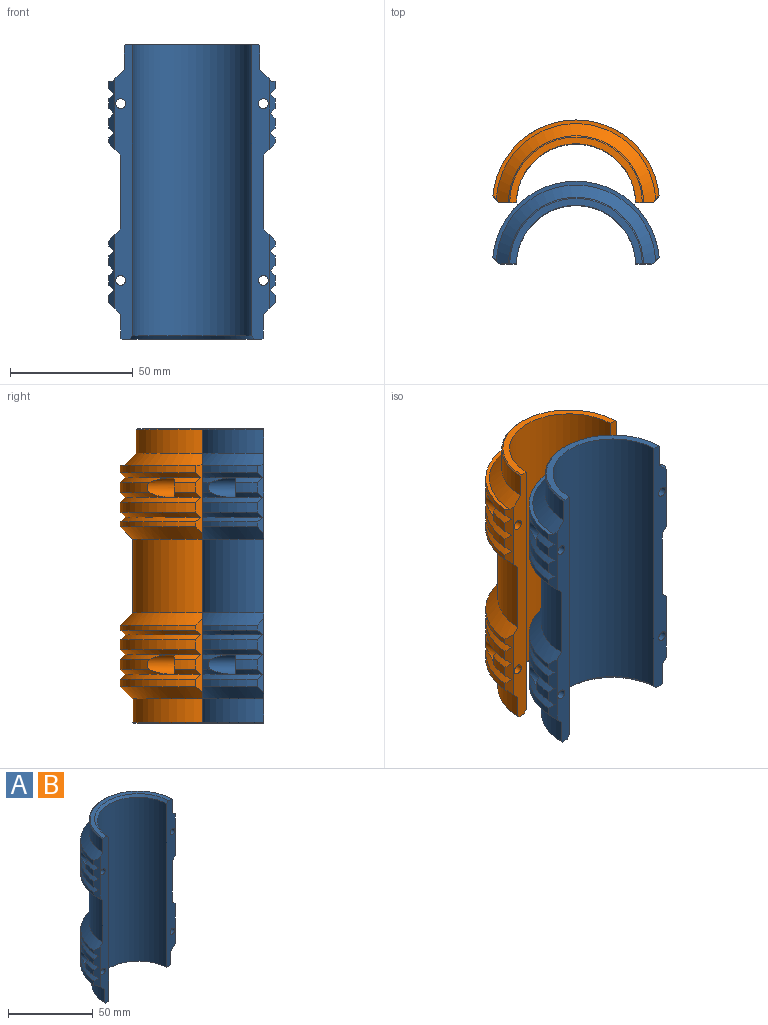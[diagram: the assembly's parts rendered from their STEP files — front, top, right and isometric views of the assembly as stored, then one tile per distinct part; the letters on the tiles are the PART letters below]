
ASSEMBLY  parts=2 mates=1
PART A: 64 faces, bbox 68.1x33.7x120.1 mm
  f0: cone r=32mm half-angle=45deg, axis (0,0,1), area 175.5mm2, adj f4,f42,f54,f60
  f1: cone r=35mm half-angle=45deg, axis (0,0,-1), area 175.5mm2, adj f4,f43,f54,f60
  f2: cone r=32mm half-angle=45deg, axis (0,0,1), area 175.5mm2, adj f7,f48,f52,f58
  f3: cone r=35mm half-angle=45deg, axis (0,0,-1), area 175.5mm2, adj f7,f49,f52,f58
  f4: cylinder r=34mm len=51.17mm, axis (0,0,-1), area 227.3mm2, adj f0,f1,f54,f60
  f5: cylinder r=34mm len=8.81mm, axis (0,0,-1), area 36.3mm2, adj f8,f10,f40,f61
  f6: cylinder r=34mm len=8.81mm, axis (0,0,-1), area 36.3mm2, adj f12,f14,f41,f59
  f7: cylinder r=34mm len=51.17mm, axis (0,0,-1), area 227.3mm2, adj f2,f3,f52,f58
  f8: cone r=32mm half-angle=45deg, axis (0,0,1), area 28.7mm2, adj f5,f40,f42,f60,f61
  f9: cone r=32mm half-angle=45deg, axis (0,0,1), area 28.7mm2, adj f20,f39,f42,f54,f55
  f10: cone r=35mm half-angle=45deg, axis (0,0,-1), area 28.7mm2, adj f5,f40,f43,f60,f61
  f11: cone r=35mm half-angle=45deg, axis (0,0,-1), area 28.7mm2, adj f20,f39,f43,f54,f55
  f12: cone r=32mm half-angle=45deg, axis (0,0,1), area 28.7mm2, adj f6,f41,f48,f58,f59
  f13: cone r=32mm half-angle=45deg, axis (0,0,1), area 28.7mm2, adj f16,f38,f48,f52,f53
  f14: cone r=35mm half-angle=45deg, axis (0,0,-1), area 28.7mm2, adj f6,f41,f49,f58,f59
  f15: cone r=35mm half-angle=45deg, axis (0,0,-1), area 28.7mm2, adj f16,f38,f49,f52,f53
  f16: cylinder r=34mm len=8.81mm, axis (0,0,-1), area 36.3mm2, adj f13,f15,f38,f53
  f17: cylinder r=34mm len=67.7mm, axis (0,0,-1), area 401.7mm2, adj f38,f41,f47,f48
  f18: cylinder r=34mm len=67.7mm, axis (0,0,-1), area 200.8mm2, adj f37,f38,f41,f46
  f19: cylinder r=34mm len=67.7mm, axis (0,0,-1), area 401.7mm2, adj f39,f40,f43,f44
  f20: cylinder r=34mm len=8.81mm, axis (0,0,-1), area 36.3mm2, adj f9,f11,f39,f55
  f21: cylinder r=34mm len=67.7mm, axis (0,0,-1), area 301.2mm2, adj f29,f39,f40,f42
  f22: plane 120x7.16mm, normal (0,-1,0), area 680.4mm2, adj f24,f25,f26,f27,f30,f31,f32,f34
  f23: cylinder r=34mm len=67.7mm, axis (0,0,-1), area 301.2mm2, adj f36,f38,f41,f49
  f24: cone r=24.25mm half-angle=45deg, axis (0,0,1), area 164.5mm2, adj f22,f25,f30,f33
  f25: cylinder r=24.25mm len=118.5mm, axis (0,0,1), area 8909.3mm2, adj f22,f24,f26,f33
  f26: plane 53.99x26.5mm, normal (0,0,-1), area 218.6mm2, adj f22,f25,f33,f62
  f27: cylinder r=27.5mm len=54.99mm, axis (0,0,-1), area 811.2mm2, adj f22,f33,f34,f62
  f28: cylinder r=34mm len=67.7mm, axis (0,0,-1), area 200.8mm2, adj f35,f39,f40,f45
  f29: plane 67.7x32.34mm, normal (0,0,-1), area 149.4mm2, adj f21,f34,f39,f40
  f30: plane 56.99x28mm, normal (0,0,1), area 231.6mm2, adj f22,f24,f33,f63
  f31: cylinder r=29mm len=57.99mm, axis (0,0,-1), area 856mm2, adj f22,f33,f36,f63
  f32: cylinder r=29mm len=57.99mm, axis (0,0,-1), area 2703.2mm2, adj f22,f33,f35,f37
  f33: plane 120x7.16mm, normal (0,-1,0), area 680.4mm2, adj f24,f25,f26,f27,f30,f31,f32,f34
  f34: cone r=27.5mm half-angle=45deg, axis (0,0,1), area 657.6mm2, adj f22,f27,f29,f33,f39,f40
  f35: cone r=34mm half-angle=45deg, axis (0,0,-1), area 683mm2, adj f22,f28,f32,f33,f39,f40
  f36: cone r=34mm half-angle=45deg, axis (0,0,-1), area 683mm2, adj f22,f23,f31,f33,f38,f41
  f37: cone r=29mm half-angle=45deg, axis (0,0,1), area 683mm2, adj f18,f22,f32,f33,f38,f41
  f38: plane 30.33x2.82mm, normal (-0.74,-0.67,0), area 84.2mm2, adj f13,f15,f16,f17,f18,f23,f33,f36
  f39: plane 28.83x2.82mm, normal (-0.74,-0.67,0), area 80.3mm2, adj f9,f11,f19,f20,f21,f28,f29,f33
  f40: plane 28.83x2.82mm, normal (0.74,-0.67,0), area 80.3mm2, adj f5,f8,f10,f19,f21,f22,f28,f29
  f41: plane 30.33x2.82mm, normal (0.74,-0.67,0), area 84.2mm2, adj f6,f12,f14,f17,f18,f22,f23,f36
  f42: cone r=35mm half-angle=45deg, axis (0,0,-1), area 281.1mm2, adj f0,f8,f9,f21,f39,f40
  f43: cone r=32mm half-angle=45deg, axis (0,0,1), area 281.1mm2, adj f1,f10,f11,f19,f39,f40
  f44: cone r=35mm half-angle=45deg, axis (0,0,-1), area 281.1mm2, adj f19,f39,f40,f45
  f45: cone r=32mm half-angle=45deg, axis (0,0,1), area 281.1mm2, adj f28,f39,f40,f44
  f46: cone r=35mm half-angle=45deg, axis (0,0,-1), area 281.1mm2, adj f18,f38,f41,f47
  f47: cone r=32mm half-angle=45deg, axis (0,0,1), area 281.1mm2, adj f17,f38,f41,f46
  f48: cone r=35mm half-angle=45deg, axis (0,0,-1), area 281.1mm2, adj f2,f12,f13,f17,f38,f41
  f49: cone r=32mm half-angle=45deg, axis (0,0,1), area 281.1mm2, adj f3,f14,f15,f23,f38,f41
  f50: cylinder r=2mm len=11.5mm, axis (0,-1,0), area 144.5mm2, adj f33,f55
  f51: cylinder r=2mm len=11.5mm, axis (0,-1,0), area 144.5mm2, adj f33,f53
  f52: cylinder r=4mm len=10.99mm, axis (0,1,0), area 95.7mm2, adj f2,f3,f7,f13,f15,f53
  f53: plane 8.02x6.79mm, normal (0,1,0), area 30.4mm2, adj f13,f15,f16,f51,f52
  f54: cylinder r=4mm len=10.99mm, axis (0,1,0), area 95.7mm2, adj f0,f1,f4,f9,f11,f55
  f55: plane 8.02x6.79mm, normal (0,1,0), area 30.4mm2, adj f9,f11,f20,f50,f54
  f56: cylinder r=2mm len=11.5mm, axis (0,-1,0), area 144.5mm2, adj f22,f61
  f57: cylinder r=2mm len=11.5mm, axis (0,-1,0), area 144.5mm2, adj f22,f59
  f58: cylinder r=4mm len=10.99mm, axis (0,1,0), area 95.7mm2, adj f2,f3,f7,f12,f14,f59
  f59: plane 8.02x6.79mm, normal (0,1,0), area 30.4mm2, adj f6,f12,f14,f57,f58
  f60: cylinder r=4mm len=10.99mm, axis (0,1,0), area 95.7mm2, adj f0,f1,f4,f8,f10,f61
  f61: plane 8.02x6.79mm, normal (0,1,0), area 30.4mm2, adj f5,f8,f10,f56,f60
  f62: cone r=27mm half-angle=45deg, axis (0,0,1), area 59.8mm2, adj f22,f26,f27,f33
  f63: cone r=29mm half-angle=45deg, axis (0,0,-1), area 63.2mm2, adj f22,f30,f31,f33
PART B: same geometry as A
PLACE A rot(axis=(0,1,0),180deg) t=(-81.18,-34.98,91.7)mm fixed
PLACE B rot(axis=(0,1,0),180deg) t=(-81.18,-9.98,91.7)mm
MATE fastened A.f26 <-> B.f26  axis (0,0,-1) through (-105.43,-34.48,91.7)mm
